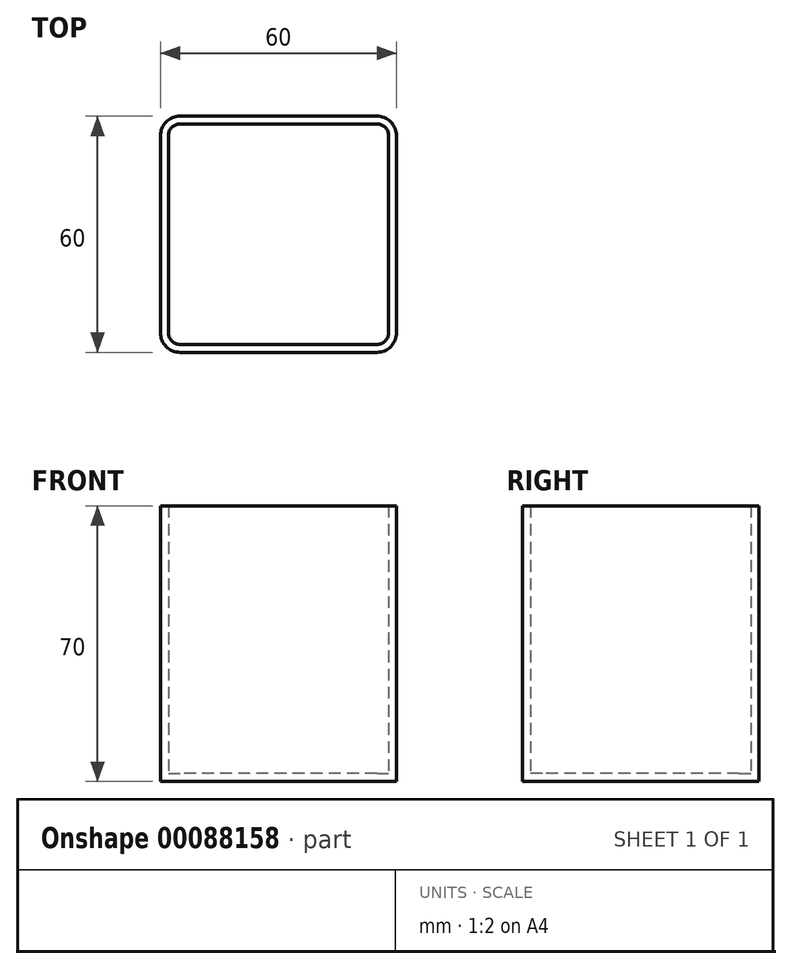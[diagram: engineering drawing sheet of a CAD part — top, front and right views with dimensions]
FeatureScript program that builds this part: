
annotation { "Feature Type Name" : "Feature", "Feature Type Description" : "" }
export const myFeature = defineFeature(function(context is Context, id is Id, definition is map)
    precondition{}
    {
        {
            assignVariable(context, id + "F0", {"name" : "thickness", "anyValue" : 2});
        }
        {
            assignVariable(context, id + "F1", {"name" : "fillet", "anyValue" : 5});
        }
        {
            var Q0;
            Q0=qCreatedBy(makeId("Top.planeOp"),FACE);
            var sketch = newSketch(context, id + "F2", { "sketchPlane" : qUnion([Q0])});
            skLineSegment(sketch, "E0.bottom", {"start": v(30, 30) * mm, "end": v(-30, 30) * mm});
            skLineSegment(sketch, "E0.top", {"start": v(30, -30) * mm, "end": v(-30, -30) * mm});
            skLineSegment(sketch, "E0.left", {"start": v(30, 30) * mm, "end": v(30, -30) * mm});
            skLineSegment(sketch, "E0.right", {"start": v(-30, 30) * mm, "end": v(-30, -30) * mm});
            skPoint(sketch, "E0.middle", {"position": v(0, 0) * mm});
            skLineSegment(sketch, "E1.bottom", {"start": v(28, 28) * mm, "end": v(-28, 28) * mm});
            skLineSegment(sketch, "E1.top", {"start": v(28, -28) * mm, "end": v(-28, -28) * mm});
            skLineSegment(sketch, "E1.left", {"start": v(28, 28) * mm, "end": v(28, -28) * mm});
            skLineSegment(sketch, "E1.right", {"start": v(-28, 28) * mm, "end": v(-28, -28) * mm});
            skSolve(sketch);
        }
        {
            var Q0;
            Q0=makeQuery(id+"F2.imprint","IMPRINT",FACE,{"disambiguationData":[TD([[makeQuery(id+"F2.imprint","IMPRINT",EDGE,{"derivedFrom":sQuery(id+"F2.wireOp",EDGE,"E1.bottom")}),1.0]])]});
            extrude(context, id + "F3", {"entities" : qUnion([Q0]), "depth" : (getVariable(context, 'thickness')) * mm});
        }
        {
            var Q0;
            Q0=makeQuery(id+"F2.imprint","IMPRINT",FACE,{"disambiguationData":[TD([[makeQuery(id+"F2.imprint","IMPRINT",EDGE,{"derivedFrom":sQuery(id+"F2.wireOp",EDGE,"E0.bottom")}),1.0]])]});
            extrude(context, id + "F4", {"entities" : qUnion([Q0]), "operationType" : NewBodyOperationType.ADD, "depth" : 70 * mm});
        }
        {
            var Q0;
            Q0=makeQuery(id+"F4.opExtrude","SWEPT_EDGE",EDGE,{"disambiguationData":[OSD([sQuery(id+"F2.wireOp",EDGE,"E0.top"),sQuery(id+"F2.wireOp",EDGE,"E0.left")])]});
            var Q1;
            Q1=makeQuery(id+"F4.opExtrude","SWEPT_EDGE",EDGE,{"disambiguationData":[OSD([sQuery(id+"F2.wireOp",EDGE,"E0.top"),sQuery(id+"F2.wireOp",EDGE,"E0.right")])]});
            var Q2;
            Q2=makeQuery(id+"F4.opExtrude","SWEPT_EDGE",EDGE,{"disambiguationData":[OSD([sQuery(id+"F2.wireOp",EDGE,"E0.bottom"),sQuery(id+"F2.wireOp",EDGE,"E0.left")])]});
            var Q3;
            Q3=makeQuery(id+"F4.opExtrude","SWEPT_EDGE",EDGE,{"disambiguationData":[OSD([sQuery(id+"F2.wireOp",EDGE,"E0.bottom"),sQuery(id+"F2.wireOp",EDGE,"E0.right")])]});
            fillet(context, id + "F5", {"entities" : qUnion([Q0, Q1, Q2, Q3]), "radius" : (getVariable(context, 'fillet')) * mm, "allowEdgeOverflow" : false});
        }
        {
            var Q0;
            Q0=makeQuery(id+"F4.opExtrude","SWEPT_EDGE",EDGE,{"disambiguationData":[OSD([sQuery(id+"F2.wireOp",EDGE,"E1.bottom"),sQuery(id+"F2.wireOp",EDGE,"E1.right")])]});
            var Q1;
            Q1=makeQuery(id+"F4.opExtrude","SWEPT_EDGE",EDGE,{"disambiguationData":[OSD([sQuery(id+"F2.wireOp",EDGE,"E1.bottom"),sQuery(id+"F2.wireOp",EDGE,"E1.left")])]});
            var Q2;
            Q2=makeQuery(id+"F4.opExtrude","SWEPT_EDGE",EDGE,{"disambiguationData":[OSD([sQuery(id+"F2.wireOp",EDGE,"E1.top"),sQuery(id+"F2.wireOp",EDGE,"E1.left")])]});
            var Q3;
            Q3=makeQuery(id+"F4.opExtrude","SWEPT_EDGE",EDGE,{"disambiguationData":[OSD([sQuery(id+"F2.wireOp",EDGE,"E1.top"),sQuery(id+"F2.wireOp",EDGE,"E1.right")])]});
            fillet(context, id + "F6", {"entities" : qUnion([Q0, Q1, Q2, Q3]), "radius" : (getVariable(context, 'fillet') - getVariable(context, 'thickness')) * mm, "tangentPropagation" : true, "allowEdgeOverflow" : false});
        }
    });
